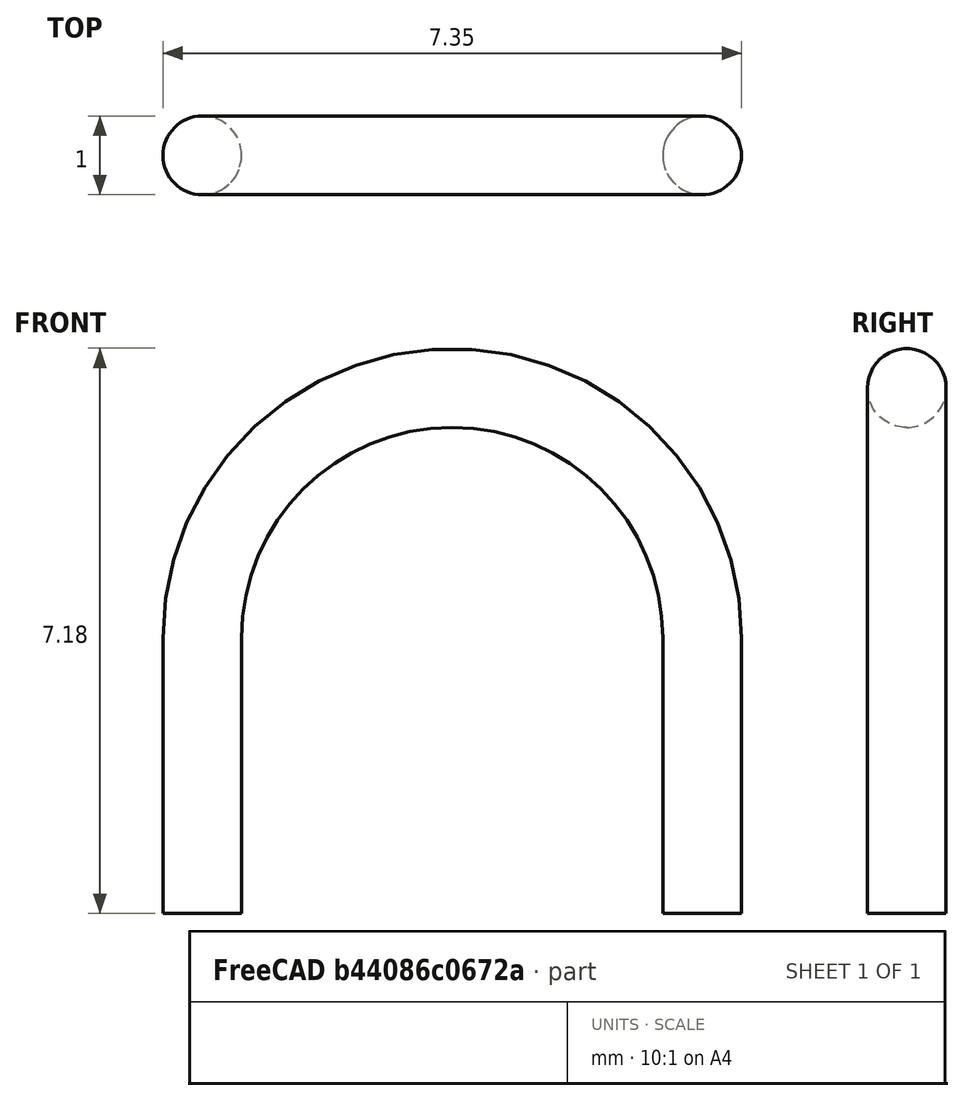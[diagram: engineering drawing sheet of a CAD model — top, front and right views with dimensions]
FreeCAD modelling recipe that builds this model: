
FCSTD DOCUMENT  (FreeCAD 0.17R12018 (Git))
Label: Test_Point_Bridge_Pitch6.35mm_Drill1.3mm
License: All rights reserved
LicenseURL: http://en.wikipedia.org/wiki/All_rights_reserved
objects: Sketcher::SketchObject×2, Spreadsheet::Sheet×1, PartDesign::SubtractivePipe×1, PartDesign::Body×1
note: 5 computed .brp shape members not serialized (recipe doc carries the construction recipe); baked Part::Feature solids carry a one-line shape summary decoded from their .brp

FEATURE [Sketcher::SketchObject] Sketch
  MapMode = 5
  Placement = pos=(0,0,-3) rot=(0,0,1;0rad)
  Support = -> [XY_Plane]
  superPlacement = pos=(0,0,-3) rot=(0,0,1;0rad)
  expr: Constraints[1] = dims.DWire / 2
  sketch-geometry (1):
    g0: Circle CenterX=0 CenterY=0 CenterZ=0 NormalX=0 NormalY=0 NormalZ=1 Radius=0.5
  constraints (2):
    c: Coincident(g0,g-1)
    c: Radius(g0) = 0.5
FEATURE [Spreadsheet::Sheet] Spreadsheet  label="dims"
  cells = A1="DWire"; B1(DWire)=1; A2="Pitch"; B2(Pitch)=6.3499999999999996
FEATURE [Sketcher::SketchObject] Sketch001
  MapMode = 5
  Placement = pos=(0,0,0) rot=(1,0,0;1.5708rad)
  Support = -> [XZ_Plane]
  expr: Constraints[10] = dims.DWire / 2
  expr: Constraints[3] = dims.Pitch
  sketch-geometry (4):
    g0: LineSegment StartX=0 StartY=-3 StartZ=0 EndX=0 EndY=0.5 EndZ=0
    g1: LineSegment StartX=6.35 StartY=0.5 StartZ=0 EndX=6.35 EndY=-3 EndZ=0
    g2: LineSegment [constr] StartX=0 StartY=0.5 StartZ=0 EndX=6.35 EndY=0.5 EndZ=0
    g3: ArcOfCircle CenterX=3.175 CenterY=0.5 CenterZ=0 NormalX=0 NormalY=0 NormalZ=1 Radius=3.175 StartAngle=0 EndAngle=3.14159
  constraints (13):
    c: PointOnObject(g0,g-2)
    c: Vertical(g0)
    c: Vertical(g1)
    c: DistanceX(g0,g1) = 6.35
    c: Coincident(g2,g0)
    c: Coincident(g2,g1)
    c: Horizontal(g2)
    c: PointOnObject(g3,g2)
    c: Coincident(g3,g0)
    c: Coincident(g3,g1)
    c: DistanceY(g-1,g3) = 0.5
    c: DistanceY(g0,g-1) = 3
    c: Equal(g1,g0)
FEATURE [PartDesign::SubtractivePipe] SubtractivePipe
  AuxilleryCurvelinear = true
  AuxillerySpineTangent = false
  Binormal = (0,0,0)
  Mode = 0
  Profile = -> Sketch
  Spine = -> Sketch001
  SpineTangent = false
  Transformation = 0
  Transition = 0
FEATURE [PartDesign::Body] Body  label="Test_Point_Bridge_Pitch6.35mm_Drill1.3mm"
  Group = -> [Sketch,Sketch001,SubtractivePipe]
  Origin = -> Origin
  Tip = -> SubtractivePipe
